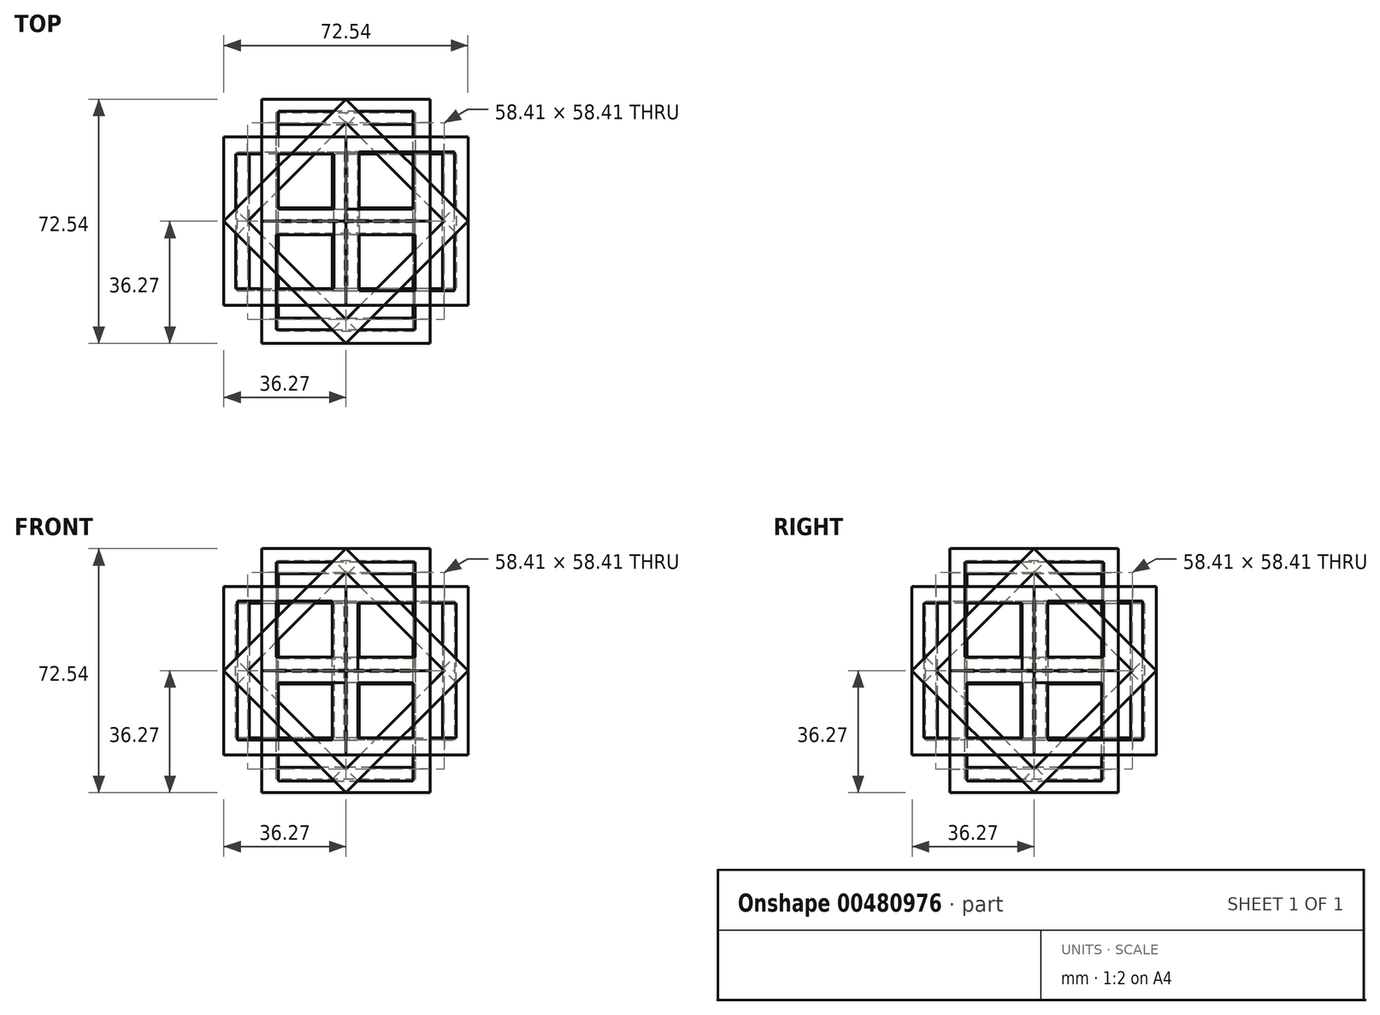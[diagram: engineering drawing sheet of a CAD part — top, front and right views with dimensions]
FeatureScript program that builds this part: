
annotation { "Feature Type Name" : "Feature", "Feature Type Description" : "" }
export const myFeature = defineFeature(function(context is Context, id is Id, definition is map)
    precondition{}
    {
        {
            var Q0;
            Q0=qCreatedBy(makeId("Front.planeOp"),FACE);
            var sketch = newSketch(context, id + "F0", { "sketchPlane" : qUnion([Q0])});
            skLineSegment(sketch, "E0", {"start": v(-36.27, 0) * mm, "end": v(0, 36.27) * mm});
            skLineSegment(sketch, "E1", {"start": v(0, 36.27) * mm, "end": v(36.27, 0) * mm});
            skLineSegment(sketch, "E2", {"start": v(36.27, 0) * mm, "end": v(0, -36.27) * mm});
            skLineSegment(sketch, "E3", {"start": v(0, -36.27) * mm, "end": v(-36.27, 0) * mm});
            skLineSegment(sketch, "E4.0", {"start": v(-29.2, 0) * mm, "end": v(0, 29.2) * mm});
            skLineSegment(sketch, "E4.1", {"start": v(0, -29.2) * mm, "end": v(-29.2, 0) * mm});
            skLineSegment(sketch, "E4.2", {"start": v(29.2, 0) * mm, "end": v(0, -29.2) * mm});
            skLineSegment(sketch, "E4.3", {"start": v(0, 29.2) * mm, "end": v(29.2, 0) * mm});
            skSolve(sketch);
        }
        {
            var Q0;
            Q0=makeQuery(id+"F0.imprint","IMPRINT",FACE,{"disambiguationData":[TD([[makeQuery(id+"F0.imprint","IMPRINT",EDGE,{"derivedFrom":sQuery(id+"F0.wireOp",EDGE,"E0")}),-1.0]])]});
            extrude(context, id + "F1", {"entities" : qUnion([Q0]), "endBound" : BoundingType.SYMMETRIC, "depth" : 50 * mm});
        }
        {
            var Q0;
            Q0=makeQuery(id+"F1.opExtrude","SWEPT_FACE",FACE,{"disambiguationData":[OSD([sQuery(id+"F0.wireOp",EDGE,"E1")])]});
            var sketch = newSketch(context, id + "F2", { "sketchPlane" : qUnion([Q0])});
            skLineSegment(sketch, "E5.0", {"start": v(20.65, 20) * mm, "end": v(-20.65, 20) * mm});
            skLineSegment(sketch, "E5.1", {"start": v(20.65, -20) * mm, "end": v(20.65, 20) * mm});
            skLineSegment(sketch, "E5.2", {"start": v(-20.65, -20) * mm, "end": v(20.65, -20) * mm});
            skLineSegment(sketch, "E5.3", {"start": v(-20.65, 20) * mm, "end": v(-20.65, -20) * mm});
            skSolve(sketch);
        }
        {
            var Q0;
            Q0=makeQuery(id+"F2.imprint","IMPRINT",FACE,{"disambiguationData":[TD([[makeQuery(id+"F2.imprint","IMPRINT",EDGE,{"derivedFrom":sQuery(id+"F2.wireOp",EDGE,"E5.0")}),1.0]])]});
            extrude(context, id + "F3", {"entities" : qUnion([Q0]), "operationType" : NewBodyOperationType.REMOVE, "endBound" : BoundingType.THROUGH_ALL, "oppositeDirection" : true, "depth" : 25 * mm});
        }
        {
            var Q0;
            Q0=makeQuery(id+"F1.opExtrude","SWEPT_FACE",FACE,{"disambiguationData":[OSD([sQuery(id+"F0.wireOp",EDGE,"E0")])]});
            var sketch = newSketch(context, id + "F4", { "sketchPlane" : qUnion([Q0])});
            skLineSegment(sketch, "E6.0", {"start": v(-20, 20.65) * mm, "end": v(-20, -20.65) * mm});
            skLineSegment(sketch, "E6.1", {"start": v(20, 20.65) * mm, "end": v(-20, 20.65) * mm});
            skLineSegment(sketch, "E6.2", {"start": v(20, -20.65) * mm, "end": v(20, 20.65) * mm});
            skLineSegment(sketch, "E6.3", {"start": v(-20, -20.65) * mm, "end": v(20, -20.65) * mm});
            skSolve(sketch);
        }
        {
            var Q0;
            Q0=makeQuery(id+"F4.imprint","IMPRINT",FACE,{"disambiguationData":[TD([[makeQuery(id+"F4.imprint","IMPRINT",EDGE,{"derivedFrom":sQuery(id+"F4.wireOp",EDGE,"E6.0")}),1.0]])]});
            extrude(context, id + "F5", {"entities" : qUnion([Q0]), "operationType" : NewBodyOperationType.REMOVE, "endBound" : BoundingType.THROUGH_ALL, "oppositeDirection" : true, "depth" : 25 * mm});
        }
        {
            var Q0;
            Q0=qCreatedBy(makeId("Top.planeOp"),FACE);
            var sketch = newSketch(context, id + "F6", { "sketchPlane" : qUnion([Q0])});
            skLineSegment(sketch, "E7", {"start": v(35.84, 0) * mm, "end": v(-36.27, 0) * mm, "construction": true});
            skSolve(sketch);
        }
        {
            var Q0;
            Q0=makeQuery(id+"F1.opExtrude","SWEPT_BODY",BODY,{"disambiguationData":[OSD([sQuery(id+"F0.wireOp",EDGE,"E0"),sQuery(id+"F0.wireOp",EDGE,"E1"),sQuery(id+"F0.wireOp",EDGE,"E2"),sQuery(id+"F0.wireOp",EDGE,"E3"),sQuery(id+"F0.wireOp",EDGE,"E4.0"),sQuery(id+"F0.wireOp",EDGE,"E4.1"),sQuery(id+"F0.wireOp",EDGE,"E4.2"),sQuery(id+"F0.wireOp",EDGE,"E4.3")])]});
            var Q1;
            Q1=sQuery(id+"F6.wireOp",EDGE,"E7");
            var Q2;
            Q2=sQuery(id+"F6.wireOp",EDGE,"E7");
            transform(context, id + "F7", {"entities" : qUnion([Q0]), "transformType" : TransformType.ROTATION, "transformAxis" : qUnion([Q2]), "angle" : 90 * degree, "makeCopy" : true});
        }
        {
            var Q0;
            Q0=qCreatedBy(makeId("Right.planeOp"),FACE);
            var sketch = newSketch(context, id + "F8", { "sketchPlane" : qUnion([Q0])});
            skLineSegment(sketch, "E8", {"start": v(-45.8, 0) * mm, "end": v(57.24, 0) * mm, "construction": true});
            skSolve(sketch);
        }
        {
            var Q0;
            Q0=makeQuery(id+"F7.opPattern","COPY",BODY,{"derivedFrom":makeQuery(id+"F1.opExtrude","SWEPT_BODY",BODY,{"disambiguationData":[OSD([sQuery(id+"F0.wireOp",EDGE,"E0"),sQuery(id+"F0.wireOp",EDGE,"E1"),sQuery(id+"F0.wireOp",EDGE,"E2"),sQuery(id+"F0.wireOp",EDGE,"E3"),sQuery(id+"F0.wireOp",EDGE,"E4.0"),sQuery(id+"F0.wireOp",EDGE,"E4.1"),sQuery(id+"F0.wireOp",EDGE,"E4.2"),sQuery(id+"F0.wireOp",EDGE,"E4.3")])]}),"instanceName":"1"});
            var Q1;
            Q1=sQuery(id+"F8.wireOp",EDGE,"E8");
            transform(context, id + "F9", {"entities" : qUnion([Q0]), "transformType" : TransformType.ROTATION, "transformAxis" : qUnion([Q1]), "angle" : 90 * degree, "makeCopy" : true});
        }
    });
